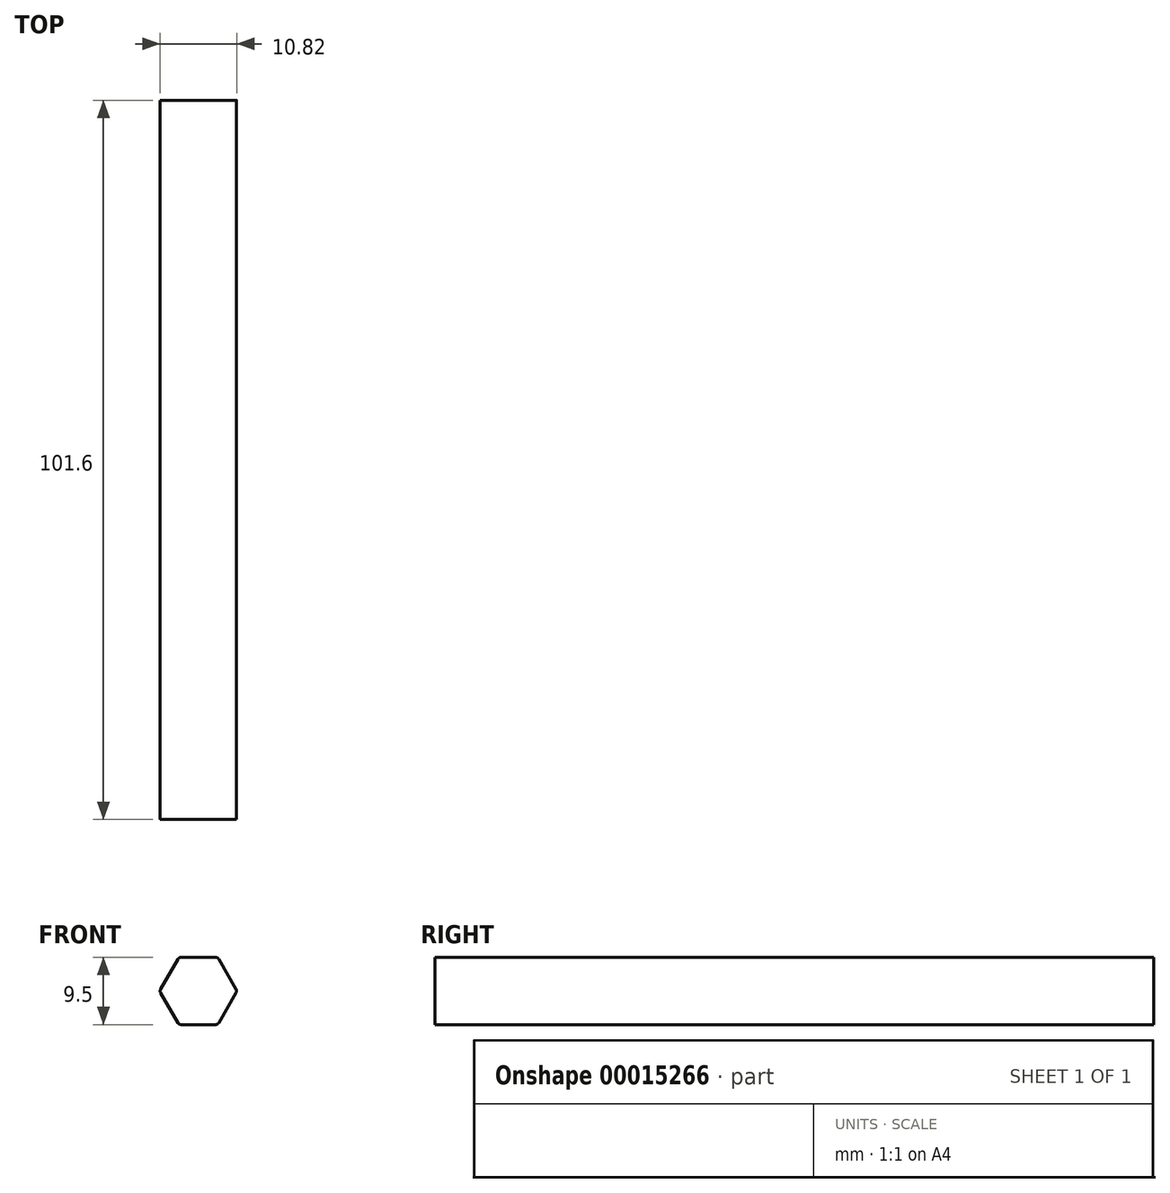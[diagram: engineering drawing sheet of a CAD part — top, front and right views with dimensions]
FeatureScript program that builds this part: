
annotation { "Feature Type Name" : "Feature", "Feature Type Description" : "" }
export const myFeature = defineFeature(function(context is Context, id is Id, definition is map)
    precondition{}
    {
        {
            var Q0;
            Q0=qCreatedBy(makeId("Front.planeOp"),FACE);
            var sketch = newSketch(context, id + "F0", { "sketchPlane" : qUnion([Q0])});
            skCircle(sketch, "E0.cCircle", {"center": v(0, 0) * mm, "radius": 4.75 * mm, "construction": true});
            skLineSegment(sketch, "E0.0", {"start": v(-2.45, 4.75) * mm, "end": v(2.45, 4.75) * mm});
            skLineSegment(sketch, "E0.1", {"start": v(2.89, 4.5) * mm, "end": v(5.34, 0.25) * mm});
            skLineSegment(sketch, "E0.2", {"start": v(5.34, -0.25) * mm, "end": v(2.89, -4.5) * mm});
            skLineSegment(sketch, "E0.3", {"start": v(2.45, -4.75) * mm, "end": v(-2.45, -4.75) * mm});
            skLineSegment(sketch, "E0.4", {"start": v(-2.89, -4.5) * mm, "end": v(-5.34, -0.25) * mm});
            skLineSegment(sketch, "E0.5", {"start": v(-5.34, 0.25) * mm, "end": v(-2.89, 4.5) * mm});
            skPoint(sketch, "E0.0.midPoint", {"position": v(0, 4.75) * mm});
            skPoint(sketch, "E1.visualSharp", {"position": v(-2.74, 4.75) * mm});
            skArc(sketch, "E1.filletArc", {"start": v(-2.45, 4.75) * mm, "mid": v(-2.7, 4.68) * mm, "end": v(-2.89, 4.5) * mm});
            skPoint(sketch, "E2.visualSharp", {"position": v(2.74, 4.75) * mm});
            skArc(sketch, "E2.filletArc", {"start": v(2.89, 4.5) * mm, "mid": v(2.7, 4.68) * mm, "end": v(2.45, 4.75) * mm});
            skPoint(sketch, "E3.visualSharp", {"position": v(5.48, 0) * mm});
            skArc(sketch, "E3.filletArc", {"start": v(5.34, -0.25) * mm, "mid": v(5.4, 0) * mm, "end": v(5.34, 0.25) * mm});
            skPoint(sketch, "E4.visualSharp", {"position": v(2.74, -4.75) * mm});
            skArc(sketch, "E4.filletArc", {"start": v(2.45, -4.75) * mm, "mid": v(2.7, -4.68) * mm, "end": v(2.89, -4.5) * mm});
            skPoint(sketch, "E5.visualSharp", {"position": v(-2.74, -4.75) * mm});
            skArc(sketch, "E5.filletArc", {"start": v(-2.89, -4.5) * mm, "mid": v(-2.7, -4.68) * mm, "end": v(-2.45, -4.75) * mm});
            skPoint(sketch, "E6.visualSharp", {"position": v(-5.48, 0) * mm});
            skArc(sketch, "E6.filletArc", {"start": v(-5.34, 0.25) * mm, "mid": v(-5.4, 0) * mm, "end": v(-5.34, -0.25) * mm});
            skSolve(sketch);
        }
        {
            var Q0;
            Q0=makeQuery(id+"F0.imprint","IMPRINT",FACE,{"disambiguationData":[TD([[makeQuery(id+"F0.imprint","IMPRINT",EDGE,{"derivedFrom":sQuery(id+"F0.wireOp",EDGE,"E0.0")}),-1.0]])]});
            extrude(context, id + "F1", {"entities" : qUnion([Q0]), "depth" : 101.6 * mm});
        }
    });
